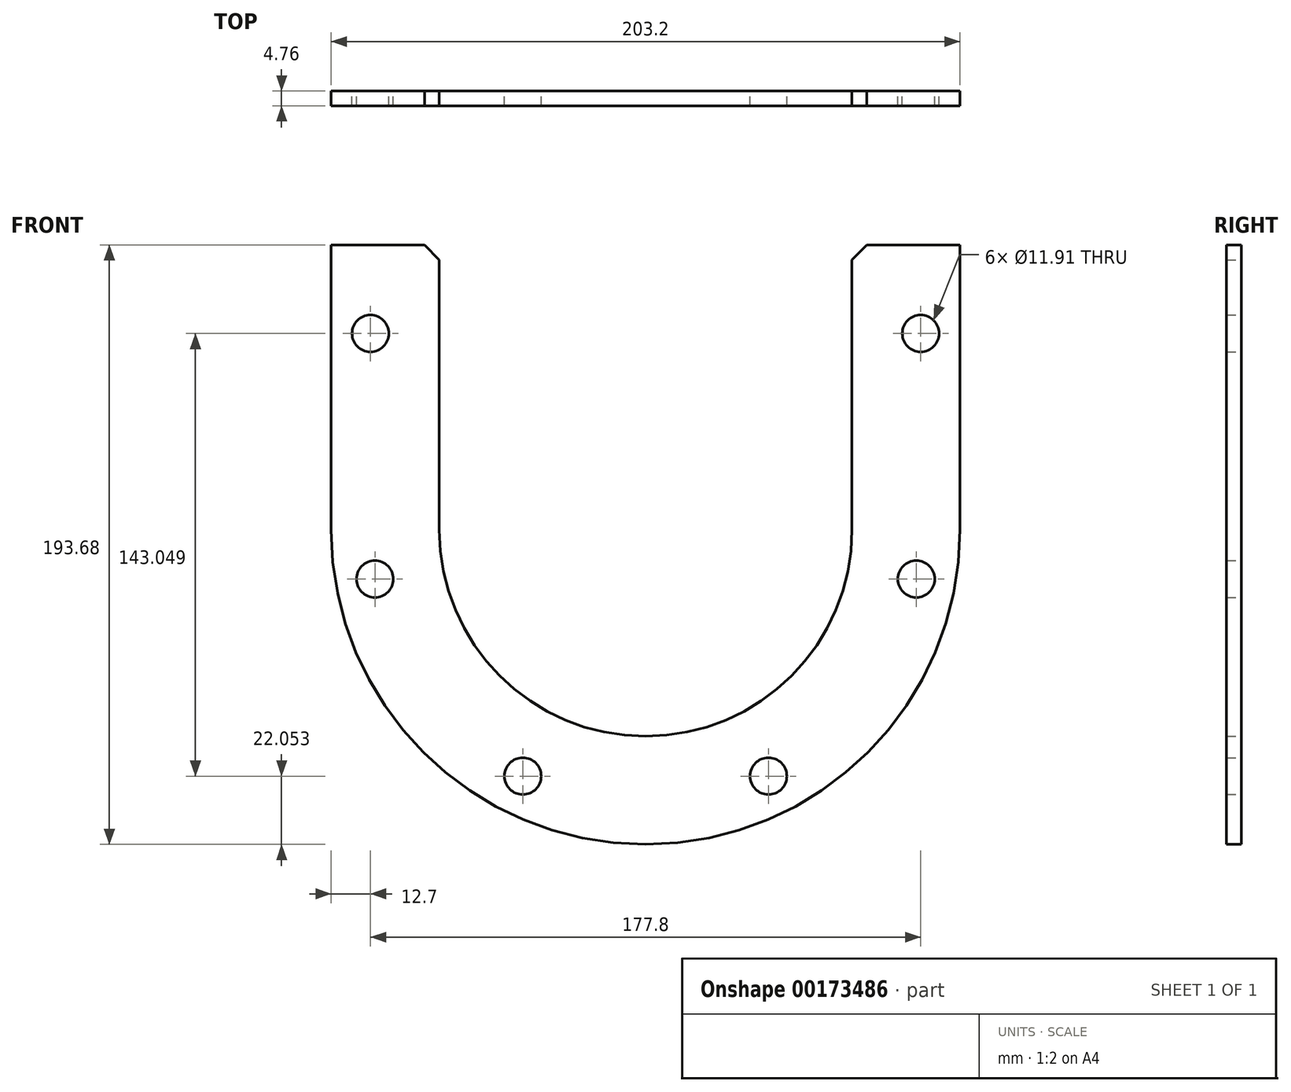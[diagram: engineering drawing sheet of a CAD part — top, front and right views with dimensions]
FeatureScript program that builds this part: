
annotation { "Feature Type Name" : "Feature", "Feature Type Description" : "" }
export const myFeature = defineFeature(function(context is Context, id is Id, definition is map)
    precondition{}
    {
        {
            var Q0;
            Q0=qCreatedBy(makeId("Front.planeOp"),FACE);
            var sketch = newSketch(context, id + "F0", { "sketchPlane" : qUnion([Q0])});
            skLineSegment(sketch, "E0", {"start": v(101.6, 96.84) * mm, "end": v(101.6, 4.76) * mm});
            skLineSegment(sketch, "E1", {"start": v(-101.6, 96.84) * mm, "end": v(-101.6, 4.76) * mm});
            skLineSegment(sketch, "E2", {"start": v(101.6, 96.84) * mm, "end": v(71.44, 96.84) * mm});
            skLineSegment(sketch, "E3", {"start": v(66.68, 92.08) * mm, "end": v(66.68, 4.76) * mm});
            skLineSegment(sketch, "E4", {"start": v(-66.68, 92.08) * mm, "end": v(-66.68, 4.76) * mm});
            skArc(sketch, "E5", {"start": v(-66.68, 4.76) * mm, "mid": v(0, -61.91) * mm, "end": v(66.68, 4.76) * mm});
            skArc(sketch, "E6", {"start": v(-101.6, 4.76) * mm, "mid": v(0, -96.84) * mm, "end": v(101.6, 4.76) * mm});
            skLineSegment(sketch, "E7", {"start": v(-71.44, 96.84) * mm, "end": v(-101.6, 96.84) * mm});
            skCircle(sketch, "E8", {"center": v(88.9, 68.26) * mm, "radius": 5.95 * mm});
            skCircle(sketch, "E9", {"center": v(87.47, -11.11) * mm, "radius": 5.95 * mm});
            skCircle(sketch, "E10", {"center": v(39.69, -74.79) * mm, "radius": 5.95 * mm});
            skCircle(sketch, "E11", {"center": v(-88.9, 68.26) * mm, "radius": 5.95 * mm});
            skCircle(sketch, "E12", {"center": v(-87.47, -11.11) * mm, "radius": 5.95 * mm});
            skCircle(sketch, "E13", {"center": v(-39.69, -74.79) * mm, "radius": 5.95 * mm});
            skLineSegment(sketch, "E14", {"start": v(66.68, 92.08) * mm, "end": v(71.44, 96.84) * mm});
            skLineSegment(sketch, "E15", {"start": v(-66.68, 92.08) * mm, "end": v(-71.44, 96.84) * mm});
            skSolve(sketch);
        }
        {
            var Q0;
            Q0 = qSketchRegion(id + "F0", true);
            extrude(context, id + "F1", {"entities" : qUnion([Q0]), "depth" : 4.76 * mm});
        }
    });
